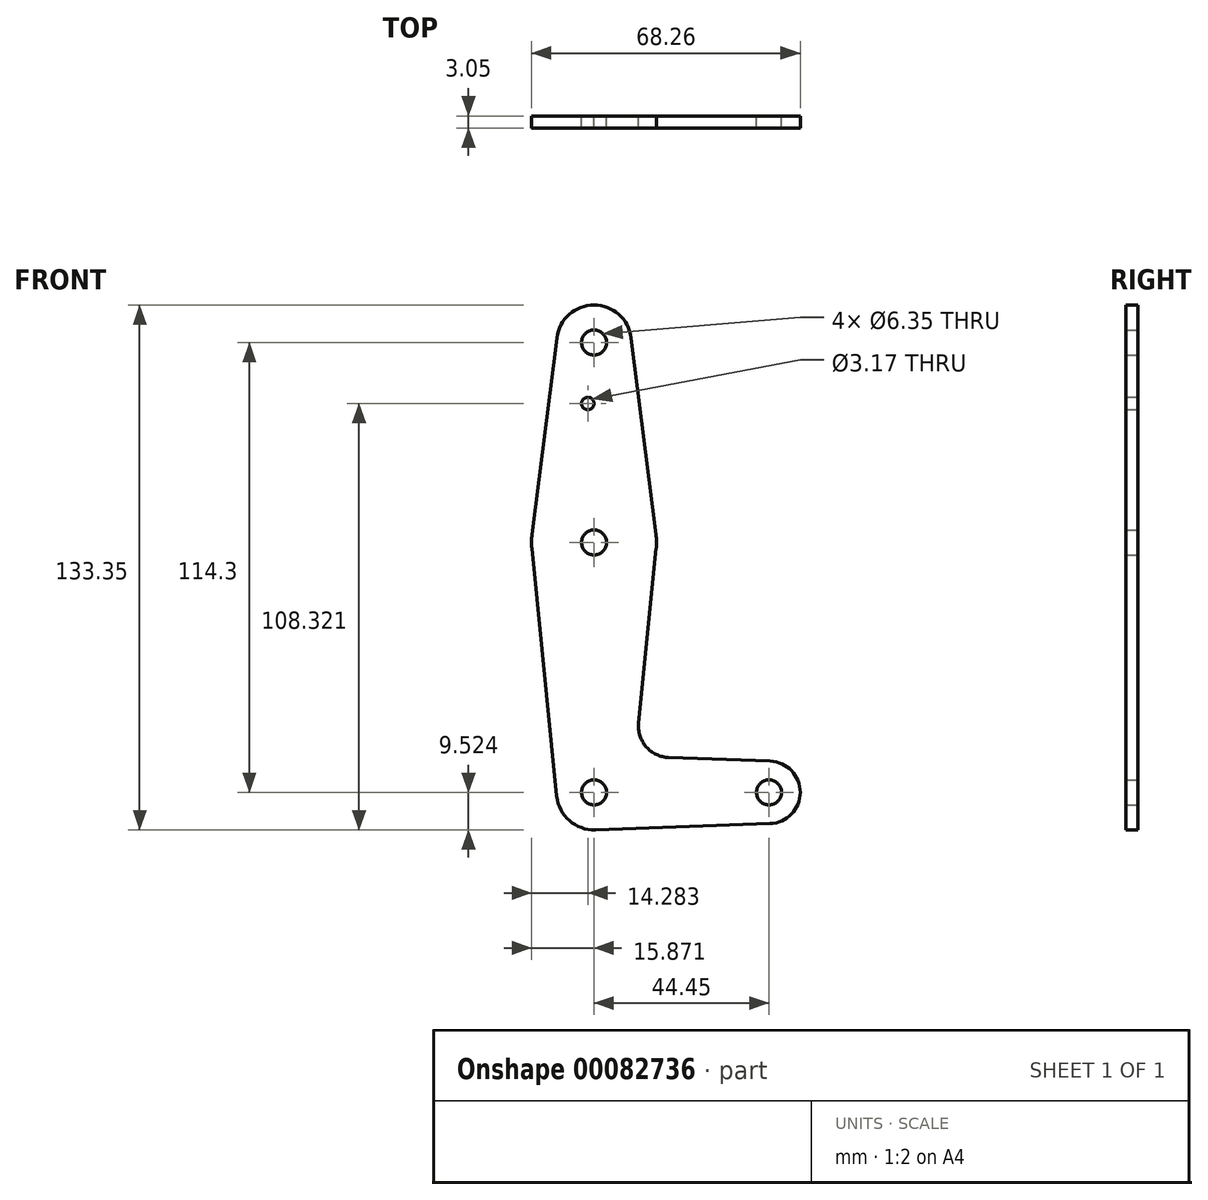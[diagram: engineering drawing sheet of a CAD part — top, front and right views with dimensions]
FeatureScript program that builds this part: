
annotation { "Feature Type Name" : "Feature", "Feature Type Description" : "" }
export const myFeature = defineFeature(function(context is Context, id is Id, definition is map)
    precondition{}
    {
        {
            var Q0;
            Q0=qCreatedBy(makeId("Front.planeOp"),FACE);
            var sketch = newSketch(context, id + "F0", { "sketchPlane" : qUnion([Q0])});
            skLineSegment(sketch, "E0", {"start": v(-58.14, 76.41) * mm, "end": v(-58.14, -37.89) * mm, "construction": true});
            skLineSegment(sketch, "E1", {"start": v(-13.69, -37.89) * mm, "end": v(-58.14, -37.89) * mm});
            skCircle(sketch, "E2", {"center": v(-58.14, 76.41) * mm, "radius": 9.53 * mm});
            skCircle(sketch, "E3", {"center": v(-58.14, -37.89) * mm, "radius": 9.53 * mm});
            skCircle(sketch, "E4", {"center": v(-13.69, -37.89) * mm, "radius": 7.94 * mm});
            skCircle(sketch, "E5", {"center": v(-58.14, 25.61) * mm, "radius": 15.88 * mm});
            skCircle(sketch, "E6", {"center": v(-58.14, 76.41) * mm, "radius": 3.18 * mm});
            skCircle(sketch, "E7", {"center": v(-58.14, 25.61) * mm, "radius": 3.18 * mm});
            skCircle(sketch, "E8", {"center": v(-58.14, -37.89) * mm, "radius": 3.18 * mm});
            skCircle(sketch, "E9", {"center": v(-13.69, -37.89) * mm, "radius": 3.18 * mm});
            skLineSegment(sketch, "E10", {"start": v(-67.59, 77.6) * mm, "end": v(-73.89, 27.6) * mm});
            skLineSegment(sketch, "E11", {"start": v(-73.93, 24.03) * mm, "end": v(-67.62, -38.84) * mm});
            skLineSegment(sketch, "E12", {"start": v(-48.69, 77.6) * mm, "end": v(-42.39, 27.6) * mm});
            skLineSegment(sketch, "E13", {"start": v(-42.34, 24.03) * mm, "end": v(-46.8, -20.3) * mm});
            skLineSegment(sketch, "E14", {"start": v(-39.17, -29.03) * mm, "end": v(-13.4, -29.95) * mm});
            skLineSegment(sketch, "E15", {"start": v(-57.8, -47.4) * mm, "end": v(-13.4, -45.82) * mm});
            skCircle(sketch, "E16", {"center": v(-59.73, 60.91) * mm, "radius": 1.59 * mm});
            skArc(sketch, "E17.filletArc", {"start": v(-46.8, -20.3) * mm, "mid": v(-44.88, -26.32) * mm, "end": v(-39.17, -29.03) * mm});
            skSolve(sketch);
        }
        {
            var Q0;
            Q0 = qSketchRegion(id + "F0", true);
            extrude(context, id + "F1", {"entities" : qUnion([Q0]), "depth" : 3.05 * mm});
        }
    });
